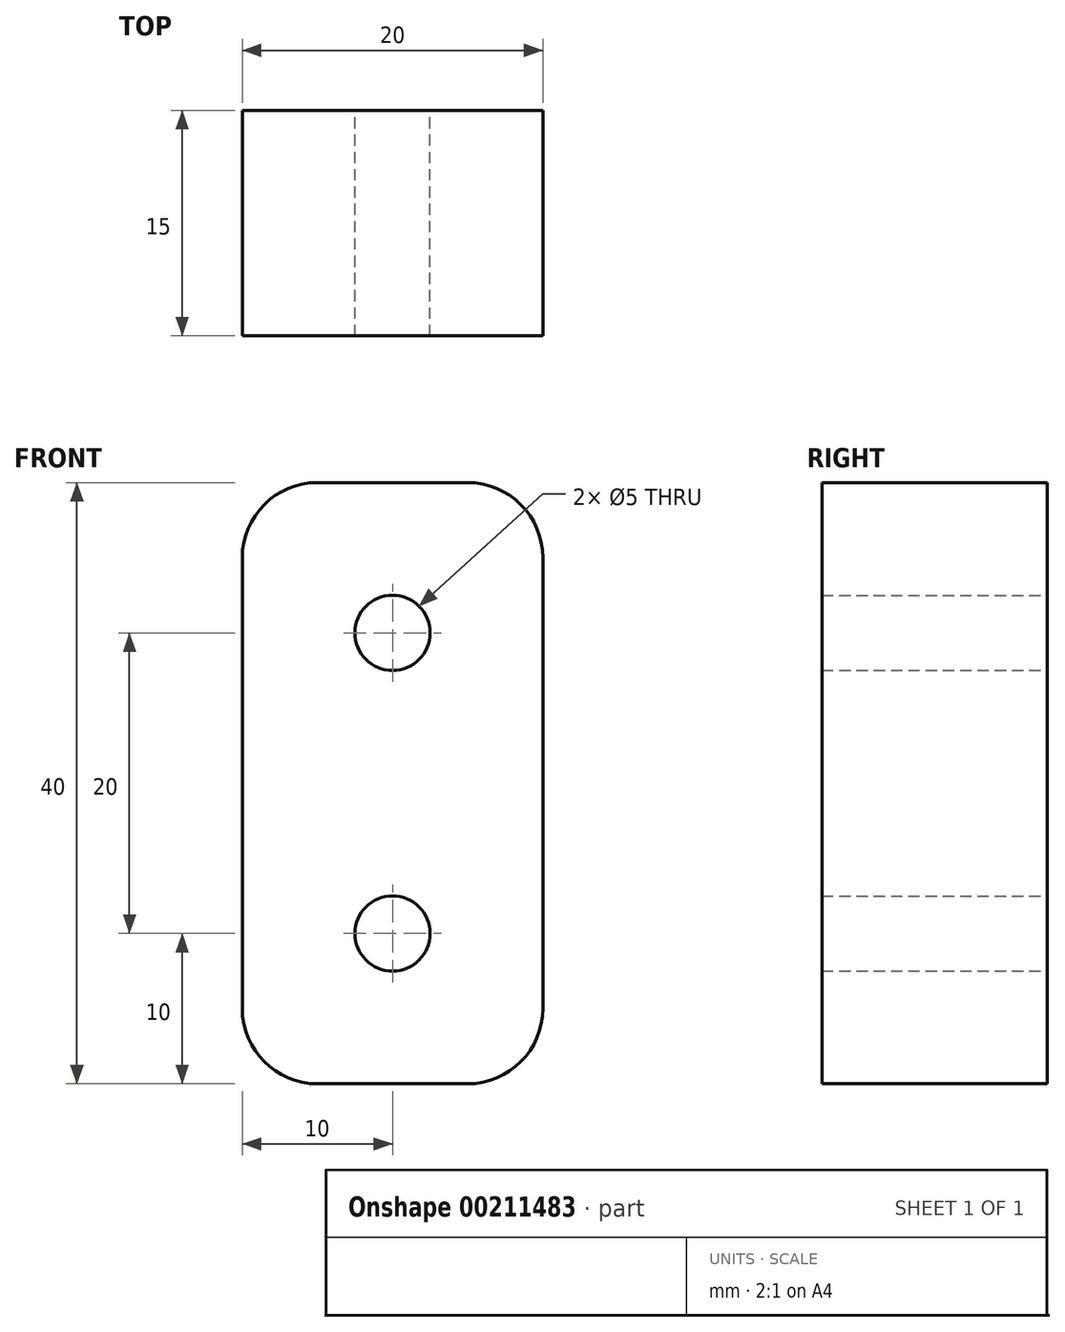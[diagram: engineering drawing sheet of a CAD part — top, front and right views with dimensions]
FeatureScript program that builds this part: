
annotation { "Feature Type Name" : "Feature", "Feature Type Description" : "" }
export const myFeature = defineFeature(function(context is Context, id is Id, definition is map)
    precondition{}
    {
        {
            var Q0;
            Q0=qCreatedBy(makeId("Front.planeOp"),FACE);
            var sketch = newSketch(context, id + "F0", { "sketchPlane" : qUnion([Q0])});
            skLineSegment(sketch, "E0.bottom", {"start": v(-10, 20) * mm, "end": v(10, 20) * mm});
            skLineSegment(sketch, "E0.top", {"start": v(-10, -20) * mm, "end": v(10, -20) * mm});
            skLineSegment(sketch, "E0.left", {"start": v(-10, 20) * mm, "end": v(-10, -20) * mm});
            skLineSegment(sketch, "E0.right", {"start": v(10, 20) * mm, "end": v(10, -20) * mm});
            skPoint(sketch, "E0.middle", {"position": v(0, 0) * mm});
            skCircle(sketch, "E1", {"center": v(0, 10) * mm, "radius": 2.5 * mm});
            skCircle(sketch, "E2", {"center": v(0, -10) * mm, "radius": 2.5 * mm});
            skSolve(sketch);
        }
        {
            var Q0;
            Q0 = qSketchRegion(id + "F0", true);
            extrude(context, id + "F1", {"entities" : qUnion([Q0]), "depth" : 15 * mm});
        }
        {
            var Q0;
            Q0=makeQuery(id+"F1.opExtrude","SWEPT_EDGE",EDGE,{"disambiguationData":[OSD([sQuery(id+"F0.wireOp",EDGE,"E0.bottom"),sQuery(id+"F0.wireOp",EDGE,"E0.left")])]});
            var Q1;
            Q1=makeQuery(id+"F1.opExtrude","SWEPT_EDGE",EDGE,{"disambiguationData":[OSD([sQuery(id+"F0.wireOp",EDGE,"E0.top"),sQuery(id+"F0.wireOp",EDGE,"E0.left")])]});
            var Q2;
            Q2=makeQuery(id+"F1.opExtrude","SWEPT_EDGE",EDGE,{"disambiguationData":[OSD([sQuery(id+"F0.wireOp",EDGE,"E0.top"),sQuery(id+"F0.wireOp",EDGE,"E0.right")])]});
            var Q3;
            Q3=makeQuery(id+"F1.opExtrude","SWEPT_EDGE",EDGE,{"disambiguationData":[OSD([sQuery(id+"F0.wireOp",EDGE,"E0.bottom"),sQuery(id+"F0.wireOp",EDGE,"E0.right")])]});
            fillet(context, id + "F2", {"entities" : qUnion([Q0, Q1, Q2, Q3]), "radius" : 5 * mm, "tangentPropagation" : true, "allowEdgeOverflow" : false});
        }
    });
